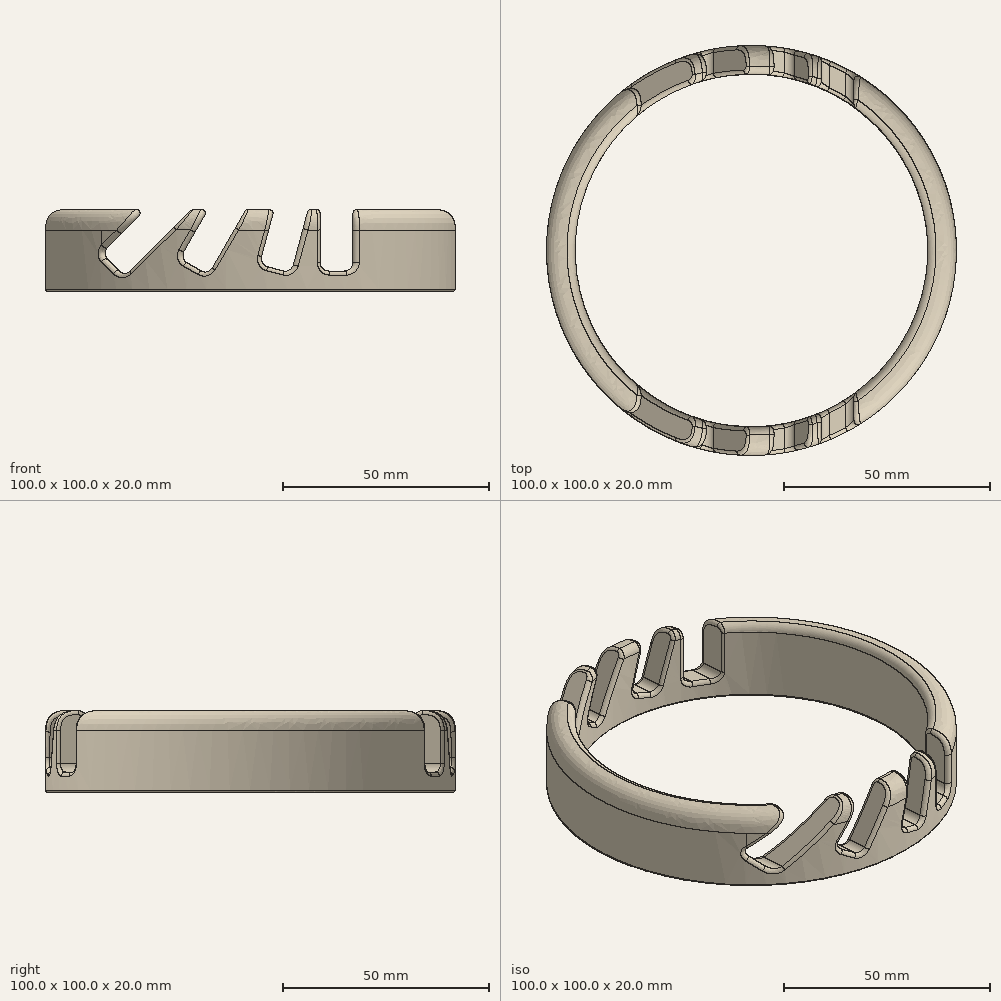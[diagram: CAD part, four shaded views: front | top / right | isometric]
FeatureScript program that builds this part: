
annotation { "Feature Type Name" : "Feature", "Feature Type Description" : "" }
export const myFeature = defineFeature(function(context is Context, id is Id, definition is map)
    precondition{}
    {
        {
            var Q0;
            Q0=qCreatedBy(makeId("Top.planeOp"),FACE);
            var sketch = newSketch(context, id + "F0", { "sketchPlane" : qUnion([Q0])});
            skCircle(sketch, "E0", {"center": v(0, 0) * mm, "radius": 50 * mm});
            skCircle(sketch, "E1", {"center": v(0, 0) * mm, "radius": 43 * mm});
            skSolve(sketch);
        }
        {
            var Q0;
            Q0=makeQuery(id+"F0.imprint","IMPRINT",FACE,{"disambiguationData":[TD([[makeQuery(id+"F0.imprint","IMPRINT",EDGE,{"derivedFrom":sQuery(id+"F0.wireOp",EDGE,"E0")}),1.0]])]});
            extrude(context, id + "F1", {"entities" : qUnion([Q0]), "depth" : 20 * mm});
        }
        {
            var Q0;
            Q0=makeQuery(id+"F1.opExtrude","CAP_EDGE",EDGE,{"disambiguationData":[OSD([sQuery(id+"F0.wireOp",EDGE,"E0")])],"isStart":false});
            fillet(context, id + "F2", {"entities" : qUnion([Q0]), "radius" : 5 * mm, "tangentPropagation" : true, "rho" : 0.5, "crossSection" : FilletCrossSection.CONIC, "allowEdgeOverflow" : false});
        }
        {
            var Q0;
            Q0=makeQuery(id+"F1.opExtrude","CAP_EDGE",EDGE,{"disambiguationData":[OSD([sQuery(id+"F0.wireOp",EDGE,"E1")])],"isStart":false});
            fillet(context, id + "F3", {"entities" : qUnion([Q0]), "radius" : 2 * mm, "tangentPropagation" : true, "allowEdgeOverflow" : false});
        }
        {
            var Q0;
            Q0=qCreatedBy(makeId("Front.planeOp"),FACE);
            var sketch = newSketch(context, id + "F4", { "sketchPlane" : qUnion([Q0])});
            skLineSegment(sketch, "E2.bottom", {"start": v(17, 155) * mm, "end": v(25, 155) * mm});
            skLineSegment(sketch, "E2.top", {"start": v(17, 5) * mm, "end": v(25, 5) * mm});
            skLineSegment(sketch, "E2.left", {"start": v(17, 155) * mm, "end": v(17, 5) * mm});
            skLineSegment(sketch, "E2.right", {"start": v(25, 155) * mm, "end": v(25, 5) * mm});
            skLineSegment(sketch, "E3", {"start": v(25, 5) * mm, "end": v(25, -6.5) * mm, "construction": true});
            skSolve(sketch);
        }
        {
            var Q0;
            Q0=makeQuery(id+"F4.imprint","IMPRINT",FACE,{"disambiguationData":[TD([[makeQuery(id+"F4.imprint","IMPRINT",EDGE,{"derivedFrom":sQuery(id+"F4.wireOp",EDGE,"E2.bottom")}),-1.0]])]});
            extrude(context, id + "F5", {"entities" : qUnion([Q0]), "endBound" : BoundingType.SYMMETRIC, "depth" : 150 * mm});
        }
        {
            var Q0;
            Q0=makeQuery(id+"F5.opExtrude","SWEPT_FACE",FACE,{"disambiguationData":[OSD([sQuery(id+"F4.wireOp",EDGE,"E2.left")])]});
            var Q1;
            Q1=makeQuery(id+"F5.opExtrude","SWEPT_FACE",FACE,{"disambiguationData":[OSD([sQuery(id+"F4.wireOp",EDGE,"E2.right")])]});
            fillet(context, id + "F6", {"entities" : qUnion([Q0, Q1]), "radius" : 2 * mm, "tangentPropagation" : true, "allowEdgeOverflow" : false});
        }
        {
            var Q0;
            Q0=makeQuery(id+"F5.opExtrude","SWEPT_BODY",BODY,{"disambiguationData":[OSD([sQuery(id+"F4.wireOp",EDGE,"E2.bottom"),sQuery(id+"F4.wireOp",EDGE,"E2.top"),sQuery(id+"F4.wireOp",EDGE,"E2.left"),sQuery(id+"F4.wireOp",EDGE,"E2.right")])]});
            var Q1;
            Q1=qCreatedBy(makeId("Right.planeOp"),FACE);
            transform(context, id + "F7", {"entities" : qUnion([Q0]), "transformType" : TransformType.TRANSLATION_DISTANCE, "transformDirection" : qUnion([Q1]), "distance" : 15 * mm, "oppositeDirection" : true, "makeCopy" : true});
        }
        {
            var Q0;
            Q0=makeQuery(id+"F7.opPattern","COPY",BODY,{"derivedFrom":makeQuery(id+"F5.opExtrude","SWEPT_BODY",BODY,{"disambiguationData":[OSD([sQuery(id+"F4.wireOp",EDGE,"E2.bottom"),sQuery(id+"F4.wireOp",EDGE,"E2.top"),sQuery(id+"F4.wireOp",EDGE,"E2.left"),sQuery(id+"F4.wireOp",EDGE,"E2.right")])]}),"instanceName":"1"});
            var Q1;
            {var subQ0=sQuery(id+"F4.wireOp",EDGE,"E2.top");Q1=makeQuery(id+"F7.opPattern","COPY",EDGE,{"derivedFrom":makeQuery(id+"F6.opFillet","BLEND_EDGE",EDGE,{"blendedFrom":[makeQuery(id+"F5.opExtrude","SWEPT_EDGE",EDGE,{"disambiguationData":[OSD([subQ0,sQuery(id+"F4.wireOp",EDGE,"E2.right")])]}),makeQuery(id+"F5.opExtrude","SWEPT_FACE",FACE,{"disambiguationData":[OSD([subQ0])]})],"blendedInto":[makeQuery(id+"F5.opExtrude","SWEPT_FACE",FACE,{"disambiguationData":[OSD([subQ0])]})]}),"instanceName":"1"});}
            transform(context, id + "F8", {"entities" : qUnion([Q0]), "transformType" : TransformType.ROTATION, "transformAxis" : qUnion([Q1]), "angle" : 15 * degree, "makeCopy" : false});
        }
        {
            var Q0;
            Q0=makeQuery(id+"F5.opExtrude","SWEPT_BODY",BODY,{"disambiguationData":[OSD([sQuery(id+"F4.wireOp",EDGE,"E2.bottom"),sQuery(id+"F4.wireOp",EDGE,"E2.top"),sQuery(id+"F4.wireOp",EDGE,"E2.left"),sQuery(id+"F4.wireOp",EDGE,"E2.right")])]});
            var Q1;
            Q1=qCreatedBy(makeId("Right.planeOp"),FACE);
            transform(context, id + "F9", {"entities" : qUnion([Q0]), "transformType" : TransformType.TRANSLATION_DISTANCE, "transformDirection" : qUnion([Q1]), "distance" : 35 * mm, "oppositeDirection" : true, "makeCopy" : true});
        }
        {
            var Q0;
            Q0=makeQuery(id+"F9.opPattern","COPY",BODY,{"derivedFrom":makeQuery(id+"F5.opExtrude","SWEPT_BODY",BODY,{"disambiguationData":[OSD([sQuery(id+"F4.wireOp",EDGE,"E2.bottom"),sQuery(id+"F4.wireOp",EDGE,"E2.top"),sQuery(id+"F4.wireOp",EDGE,"E2.left"),sQuery(id+"F4.wireOp",EDGE,"E2.right")])]}),"instanceName":"1"});
            var Q1;
            {var subQ0=sQuery(id+"F4.wireOp",EDGE,"E2.top");Q1=makeQuery(id+"F9.opPattern","COPY",EDGE,{"derivedFrom":makeQuery(id+"F6.opFillet","BLEND_EDGE",EDGE,{"blendedFrom":[makeQuery(id+"F5.opExtrude","SWEPT_EDGE",EDGE,{"disambiguationData":[OSD([subQ0,sQuery(id+"F4.wireOp",EDGE,"E2.right")])]}),makeQuery(id+"F5.opExtrude","SWEPT_FACE",FACE,{"disambiguationData":[OSD([subQ0])]})],"blendedInto":[makeQuery(id+"F5.opExtrude","SWEPT_FACE",FACE,{"disambiguationData":[OSD([subQ0])]})]}),"instanceName":"1"});}
            transform(context, id + "F10", {"entities" : qUnion([Q0]), "transformType" : TransformType.ROTATION, "transformAxis" : qUnion([Q1]), "angle" : 30 * degree, "makeCopy" : false});
        }
        {
            var Q0;
            Q0=makeQuery(id+"F5.opExtrude","SWEPT_BODY",BODY,{"disambiguationData":[OSD([sQuery(id+"F4.wireOp",EDGE,"E2.bottom"),sQuery(id+"F4.wireOp",EDGE,"E2.top"),sQuery(id+"F4.wireOp",EDGE,"E2.left"),sQuery(id+"F4.wireOp",EDGE,"E2.right")])]});
            var Q1;
            Q1=qCreatedBy(makeId("Right.planeOp"),FACE);
            transform(context, id + "F11", {"entities" : qUnion([Q0]), "transformType" : TransformType.TRANSLATION_DISTANCE, "transformDirection" : qUnion([Q1]), "distance" : 55 * mm, "oppositeDirection" : true, "makeCopy" : true});
        }
        {
            var Q0;
            Q0=makeQuery(id+"F11.opPattern","COPY",BODY,{"derivedFrom":makeQuery(id+"F5.opExtrude","SWEPT_BODY",BODY,{"disambiguationData":[OSD([sQuery(id+"F4.wireOp",EDGE,"E2.bottom"),sQuery(id+"F4.wireOp",EDGE,"E2.top"),sQuery(id+"F4.wireOp",EDGE,"E2.left"),sQuery(id+"F4.wireOp",EDGE,"E2.right")])]}),"instanceName":"1"});
            var Q1;
            Q1=makeQuery(id+"F11.opPattern","COPY",EDGE,{"derivedFrom":makeQuery(id+"F5.opExtrude","SWEPT_EDGE",EDGE,{"disambiguationData":[OSD([sQuery(id+"F4.wireOp",EDGE,"E2.top"),sQuery(id+"F4.wireOp",EDGE,"E2.right")])]}),"instanceName":"1"});
            var Q2;
            {var subQ0=sQuery(id+"F4.wireOp",EDGE,"E2.top");Q2=makeQuery(id+"F11.opPattern","COPY",EDGE,{"derivedFrom":makeQuery(id+"F6.opFillet","BLEND_EDGE",EDGE,{"blendedFrom":[makeQuery(id+"F5.opExtrude","SWEPT_EDGE",EDGE,{"disambiguationData":[OSD([subQ0,sQuery(id+"F4.wireOp",EDGE,"E2.right")])]}),makeQuery(id+"F5.opExtrude","SWEPT_FACE",FACE,{"disambiguationData":[OSD([subQ0])]})],"blendedInto":[makeQuery(id+"F5.opExtrude","SWEPT_FACE",FACE,{"disambiguationData":[OSD([subQ0])]})]}),"instanceName":"1"});}
            transform(context, id + "F12", {"entities" : qUnion([Q0]), "transformType" : TransformType.ROTATION, "transformAxis" : qUnion([Q2]), "angle" : 45 * degree, "makeCopy" : false});
        }
        {
            var Q0;
            Q0=makeQuery(id+"F5.opExtrude","SWEPT_BODY",BODY,{"disambiguationData":[OSD([sQuery(id+"F4.wireOp",EDGE,"E2.bottom"),sQuery(id+"F4.wireOp",EDGE,"E2.top"),sQuery(id+"F4.wireOp",EDGE,"E2.left"),sQuery(id+"F4.wireOp",EDGE,"E2.right")])]});
            var Q1;
            Q1=makeQuery(id+"F7.opPattern","COPY",BODY,{"derivedFrom":makeQuery(id+"F5.opExtrude","SWEPT_BODY",BODY,{"disambiguationData":[OSD([sQuery(id+"F4.wireOp",EDGE,"E2.bottom"),sQuery(id+"F4.wireOp",EDGE,"E2.top"),sQuery(id+"F4.wireOp",EDGE,"E2.left"),sQuery(id+"F4.wireOp",EDGE,"E2.right")])]}),"instanceName":"1"});
            var Q2;
            Q2=makeQuery(id+"F9.opPattern","COPY",BODY,{"derivedFrom":makeQuery(id+"F5.opExtrude","SWEPT_BODY",BODY,{"disambiguationData":[OSD([sQuery(id+"F4.wireOp",EDGE,"E2.bottom"),sQuery(id+"F4.wireOp",EDGE,"E2.top"),sQuery(id+"F4.wireOp",EDGE,"E2.left"),sQuery(id+"F4.wireOp",EDGE,"E2.right")])]}),"instanceName":"1"});
            var Q3;
            Q3=makeQuery(id+"F11.opPattern","COPY",BODY,{"derivedFrom":makeQuery(id+"F5.opExtrude","SWEPT_BODY",BODY,{"disambiguationData":[OSD([sQuery(id+"F4.wireOp",EDGE,"E2.bottom"),sQuery(id+"F4.wireOp",EDGE,"E2.top"),sQuery(id+"F4.wireOp",EDGE,"E2.left"),sQuery(id+"F4.wireOp",EDGE,"E2.right")])]}),"instanceName":"1"});
            var Q4;
            Q4=makeQuery(id+"F1.opExtrude","SWEPT_BODY",BODY,{"disambiguationData":[OSD([sQuery(id+"F0.wireOp",EDGE,"E0"),sQuery(id+"F0.wireOp",EDGE,"E1")])]});
            booleanBodies(context, id + "F13", {"operationType" : BooleanOperationType.SUBTRACTION, "tools" : qUnion([Q0, Q1, Q2, Q3]), "targets" : qUnion([Q4])});
        }
        {
            var Q0;
            Q0=makeQuery(id+"F13.opBoolean","COPY",FACE,{"disambiguationData":[OD(0.0)],"derivedFrom":makeQuery(id+"F9.opPattern","COPY",FACE,{"derivedFrom":makeQuery(id+"F5.opExtrude","SWEPT_FACE",FACE,{"disambiguationData":[OSD([sQuery(id+"F4.wireOp",EDGE,"E2.left")])]}),"instanceName":"1"})});
            var Q1;
            Q1=makeQuery(id+"F13.opBoolean","COPY",FACE,{"disambiguationData":[OD(0.0)],"derivedFrom":makeQuery(id+"F11.opPattern","COPY",FACE,{"derivedFrom":makeQuery(id+"F5.opExtrude","SWEPT_FACE",FACE,{"disambiguationData":[OSD([sQuery(id+"F4.wireOp",EDGE,"E2.left")])]}),"instanceName":"1"})});
            var Q2;
            Q2=makeQuery(id+"F13.opBoolean","COPY",FACE,{"disambiguationData":[OD(0.0)],"derivedFrom":makeQuery(id+"F11.opPattern","COPY",FACE,{"derivedFrom":makeQuery(id+"F6.opFillet","BLEND_FACE",FACE,{"disambiguationData":[OSD([sQuery(id+"F4.wireOp",EDGE,"E2.top"),sQuery(id+"F4.wireOp",EDGE,"E2.left")])]}),"instanceName":"1"})});
            var Q3;
            Q3=makeQuery(id+"F13.opBoolean","COPY",FACE,{"disambiguationData":[OD(0.0)],"derivedFrom":makeQuery(id+"F11.opPattern","COPY",FACE,{"derivedFrom":makeQuery(id+"F5.opExtrude","SWEPT_FACE",FACE,{"disambiguationData":[OSD([sQuery(id+"F4.wireOp",EDGE,"E2.top")])]}),"instanceName":"1"})});
            var Q4;
            Q4=makeQuery(id+"F13.opBoolean","COPY",FACE,{"disambiguationData":[OD(0.0)],"derivedFrom":makeQuery(id+"F7.opPattern","COPY",FACE,{"derivedFrom":makeQuery(id+"F5.opExtrude","SWEPT_FACE",FACE,{"disambiguationData":[OSD([sQuery(id+"F4.wireOp",EDGE,"E2.left")])]}),"instanceName":"1"})});
            var Q5;
            Q5=makeQuery(id+"F13.opBoolean","COPY",FACE,{"disambiguationData":[OD(0.0)],"derivedFrom":makeQuery(id+"F5.opExtrude","SWEPT_FACE",FACE,{"disambiguationData":[OSD([sQuery(id+"F4.wireOp",EDGE,"E2.left")])]})});
            var Q6;
            Q6=makeQuery(id+"F13.opBoolean","COPY",FACE,{"disambiguationData":[OD(1.0)],"derivedFrom":makeQuery(id+"F11.opPattern","COPY",FACE,{"derivedFrom":makeQuery(id+"F5.opExtrude","SWEPT_FACE",FACE,{"disambiguationData":[OSD([sQuery(id+"F4.wireOp",EDGE,"E2.left")])]}),"instanceName":"1"})});
            var Q7;
            Q7=makeQuery(id+"F13.opBoolean","COPY",FACE,{"disambiguationData":[OD(1.0)],"derivedFrom":makeQuery(id+"F9.opPattern","COPY",FACE,{"derivedFrom":makeQuery(id+"F5.opExtrude","SWEPT_FACE",FACE,{"disambiguationData":[OSD([sQuery(id+"F4.wireOp",EDGE,"E2.left")])]}),"instanceName":"1"})});
            var Q8;
            Q8=makeQuery(id+"F13.opBoolean","COPY",FACE,{"disambiguationData":[OD(1.0)],"derivedFrom":makeQuery(id+"F7.opPattern","COPY",FACE,{"derivedFrom":makeQuery(id+"F5.opExtrude","SWEPT_FACE",FACE,{"disambiguationData":[OSD([sQuery(id+"F4.wireOp",EDGE,"E2.left")])]}),"instanceName":"1"})});
            var Q9;
            Q9=makeQuery(id+"F13.opBoolean","COPY",FACE,{"disambiguationData":[OD(1.0)],"derivedFrom":makeQuery(id+"F5.opExtrude","SWEPT_FACE",FACE,{"disambiguationData":[OSD([sQuery(id+"F4.wireOp",EDGE,"E2.left")])]})});
            fillet(context, id + "F14", {"entities" : qUnion([Q0, Q1, Q2, Q3, Q4, Q5, Q6, Q7, Q8, Q9]), "radius" : 1 * mm, "tangentPropagation" : true, "allowEdgeOverflow" : false});
        }
        {
            var Q0;
            Q0=makeQuery(id+"F1.opExtrude","CAP_FACE",FACE,{"disambiguationData":[OSD([sQuery(id+"F0.wireOp",EDGE,"E0"),sQuery(id+"F0.wireOp",EDGE,"E1")])],"isStart":true});
            fillet(context, id + "F15", {"entities" : qUnion([Q0]), "radius" : 0.5 * mm, "tangentPropagation" : true, "allowEdgeOverflow" : false});
        }
    });
